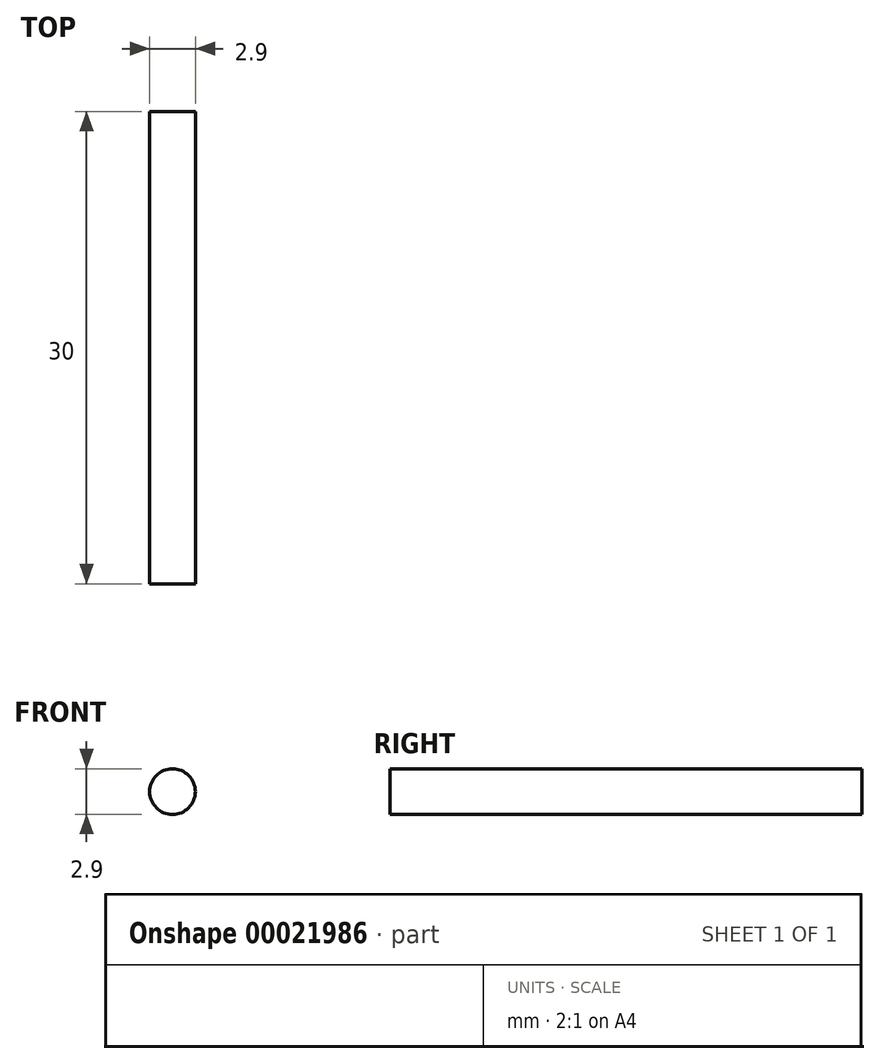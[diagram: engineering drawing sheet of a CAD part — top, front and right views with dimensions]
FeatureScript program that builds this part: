
annotation { "Feature Type Name" : "Feature", "Feature Type Description" : "" }
export const myFeature = defineFeature(function(context is Context, id is Id, definition is map)
    precondition{}
    {
        {
            var Q0;
            Q0=qCreatedBy(makeId("Front.planeOp"),FACE);
            var sketch = newSketch(context, id + "F0", { "sketchPlane" : qUnion([Q0])});
            skCircle(sketch, "E0", {"center": v(0, 0) * mm, "radius": 1.45 * mm});
            skSolve(sketch);
        }
        {
            var Q0;
            Q0 = qSketchRegion(id + "F0", true);
            extrude(context, id + "F1", {"entities" : qUnion([Q0]), "endBound" : BoundingType.SYMMETRIC, "depth" : 30 * mm});
        }
    });
